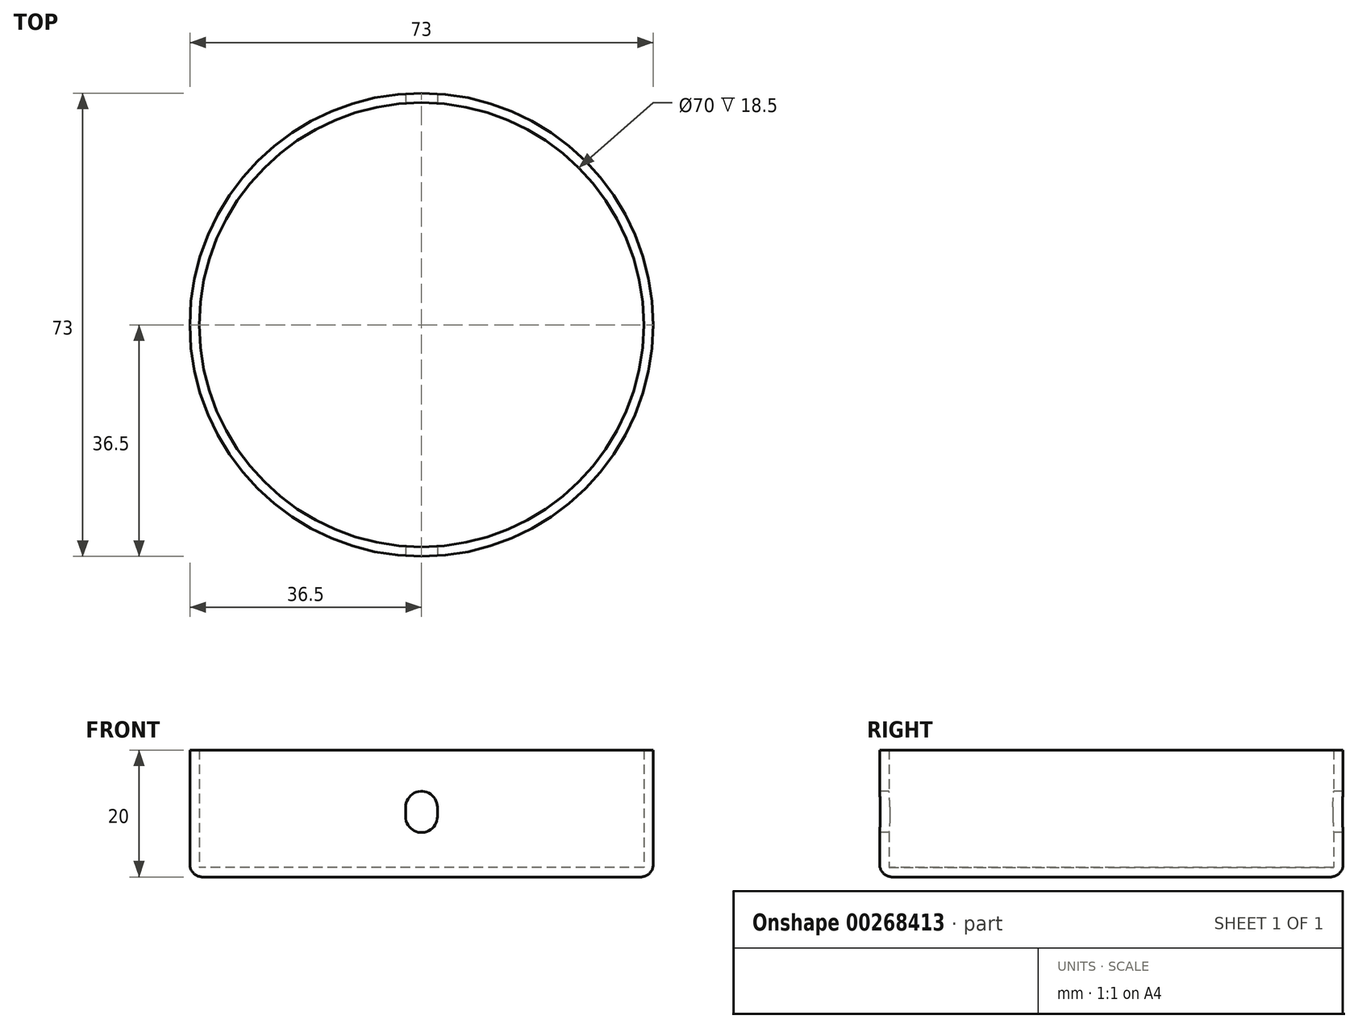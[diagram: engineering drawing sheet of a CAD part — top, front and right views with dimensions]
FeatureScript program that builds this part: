
annotation { "Feature Type Name" : "Feature", "Feature Type Description" : "" }
export const myFeature = defineFeature(function(context is Context, id is Id, definition is map)
    precondition{}
    {
        {
            var Q0;
            Q0=qCreatedBy(makeId("Top.planeOp"),FACE);
            var sketch = newSketch(context, id + "F0", { "sketchPlane" : qUnion([Q0])});
            skCircle(sketch, "E0", {"center": v(0, 0) * mm, "radius": 36.5 * mm});
            skSolve(sketch);
        }
        {
            var Q0;
            Q0 = qSketchRegion(id + "F0", true);
            extrude(context, id + "F1", {"entities" : qUnion([Q0]), "depth" : 20 * mm});
        }
        {
            var Q0;
            Q0=makeQuery(id+"F1.opExtrude","CAP_FACE",FACE,{"disambiguationData":[OSD([sQuery(id+"F0.wireOp",EDGE,"E0")])],"isStart":false});
            shell(context, id + "F2", {"entities" : qUnion([Q0]), "thickness" : 1.5 * mm});
        }
        {
            var Q0;
            Q0=makeQuery(id+"F1.opExtrude","CAP_EDGE",EDGE,{"disambiguationData":[OSD([sQuery(id+"F0.wireOp",EDGE,"E0")])],"isStart":true});
            fillet(context, id + "F3", {"entities" : qUnion([Q0]), "radius" : 2 * mm, "tangentPropagation" : true, "allowEdgeOverflow" : false});
        }
        {
            var Q0;
            Q0=qCreatedBy(makeId("Front.planeOp"),FACE);
            var sketch = newSketch(context, id + "F4", { "sketchPlane" : qUnion([Q0])});
            skArc(sketch, "E1", {"start": v(-2.5, 9.5) * mm, "mid": v(0, 7) * mm, "end": v(2.5, 9.5) * mm});
            skArc(sketch, "E2", {"start": v(2.5, 11) * mm, "mid": v(0, 13.5) * mm, "end": v(-2.5, 11) * mm});
            skLineSegment(sketch, "E3", {"start": v(-2.5, 11) * mm, "end": v(-2.5, 9.5) * mm});
            skLineSegment(sketch, "E4", {"start": v(2.5, 9.5) * mm, "end": v(2.5, 11) * mm});
            skSolve(sketch);
        }
        {
            var Q0;
            Q0 = qSketchRegion(id + "F4", true);
            extrude(context, id + "F5", {"entities" : qUnion([Q0]), "operationType" : NewBodyOperationType.REMOVE, "endBound" : BoundingType.SYMMETRIC, "oppositeDirection" : true, "depth" : 100 * mm});
        }
    });
